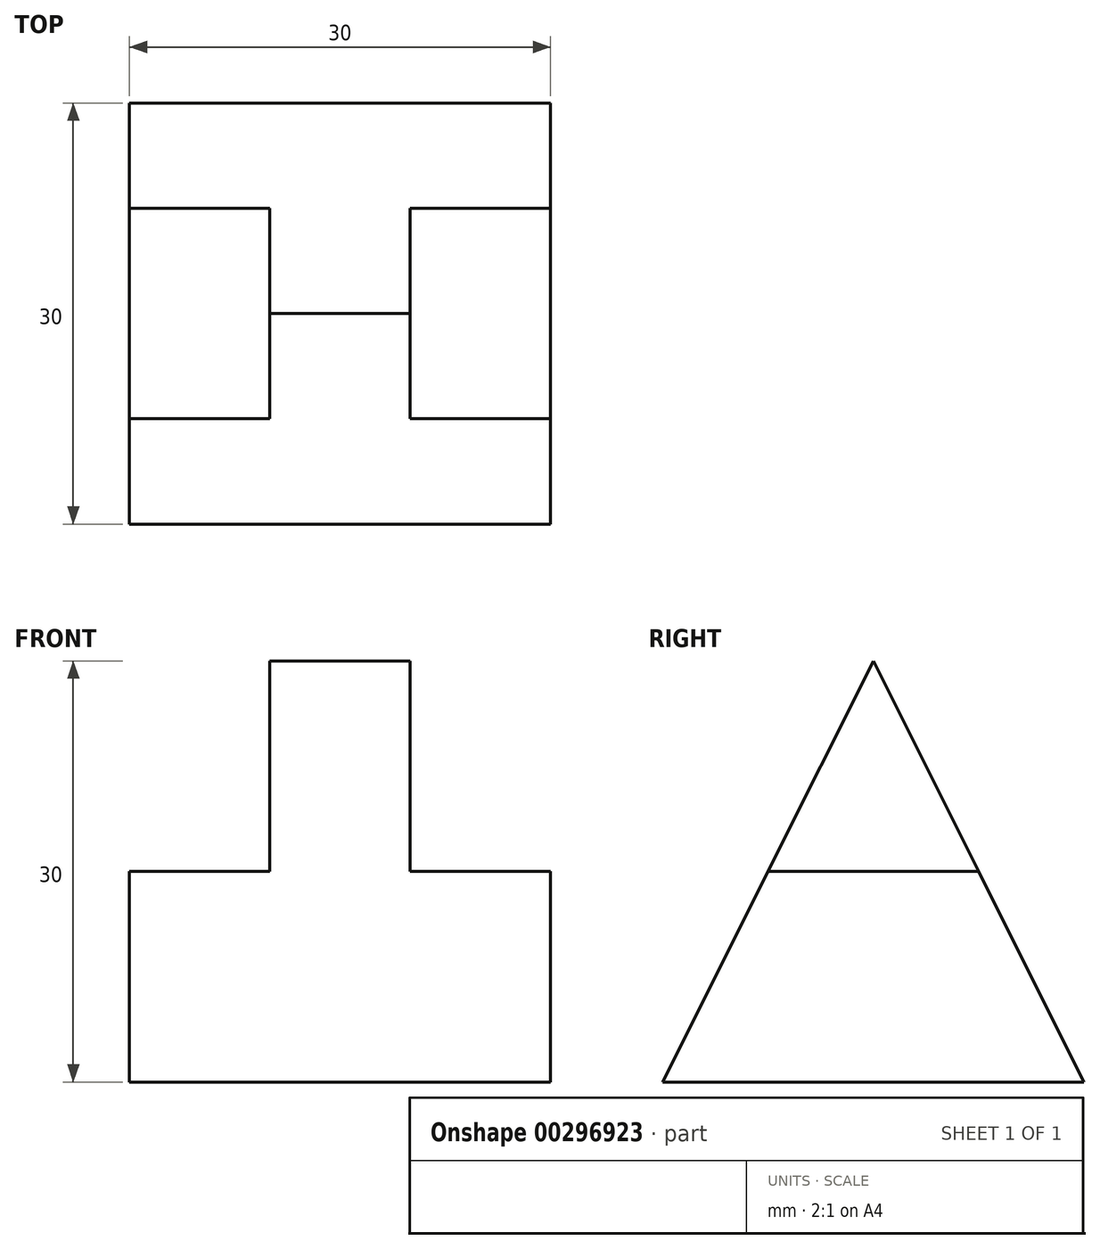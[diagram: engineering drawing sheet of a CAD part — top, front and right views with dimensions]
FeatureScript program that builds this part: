
annotation { "Feature Type Name" : "Feature", "Feature Type Description" : "" }
export const myFeature = defineFeature(function(context is Context, id is Id, definition is map)
    precondition{}
    {
        {
            var Q0;
            Q0=qCreatedBy(makeId("Right.planeOp"),FACE);
            var sketch = newSketch(context, id + "F0", { "sketchPlane" : qUnion([Q0])});
            skLineSegment(sketch, "E0.bottom", {"start": v(0, 0) * mm, "end": v(30, 0) * mm});
            skLineSegment(sketch, "E0.top", {"start": v(0, 30) * mm, "end": v(30, 30) * mm});
            skLineSegment(sketch, "E0.left", {"start": v(0, 0) * mm, "end": v(0, 30) * mm});
            skLineSegment(sketch, "E0.right", {"start": v(30, 0) * mm, "end": v(30, 30) * mm});
            skLineSegment(sketch, "E1", {"start": v(0, 0) * mm, "end": v(15, 30) * mm});
            skLineSegment(sketch, "E2", {"start": v(15, 30) * mm, "end": v(30, 0) * mm});
            skLineSegment(sketch, "E3", {"start": v(7.5, 15) * mm, "end": v(22.5, 15) * mm});
            skSolve(sketch);
        }
        {
            var Q0;
            {var subQ0=sQuery(id+"F0.wireOp",EDGE,"E0.bottom");Q0=makeQuery(id+"F0.imprint","IMPRINT",FACE,{"disambiguationData":[TD([[makeQuery(id+"F0.imprint","IMPRINT",EDGE,{"derivedFrom":subQ0}),1.0]])]});}
            extrude(context, id + "F1", {"entities" : qUnion([Q0]), "depth" : 30 * mm, "symmetric" : true});
        }
        {
            var Q0;
            {var subQ3=sQuery(id+"F0.wireOp",EDGE,"E3");Q0=makeQuery(id+"F0.imprint","IMPRINT",FACE,{"disambiguationData":[TD([[makeQuery(id+"F0.imprint","IMPRINT",EDGE,{"derivedFrom":subQ3}),1.0]])]});}
            extrude(context, id + "F2", {"entities" : qUnion([Q0]), "operationType" : NewBodyOperationType.ADD, "depth" : 10 * mm, "symmetric" : true});
        }
    });
